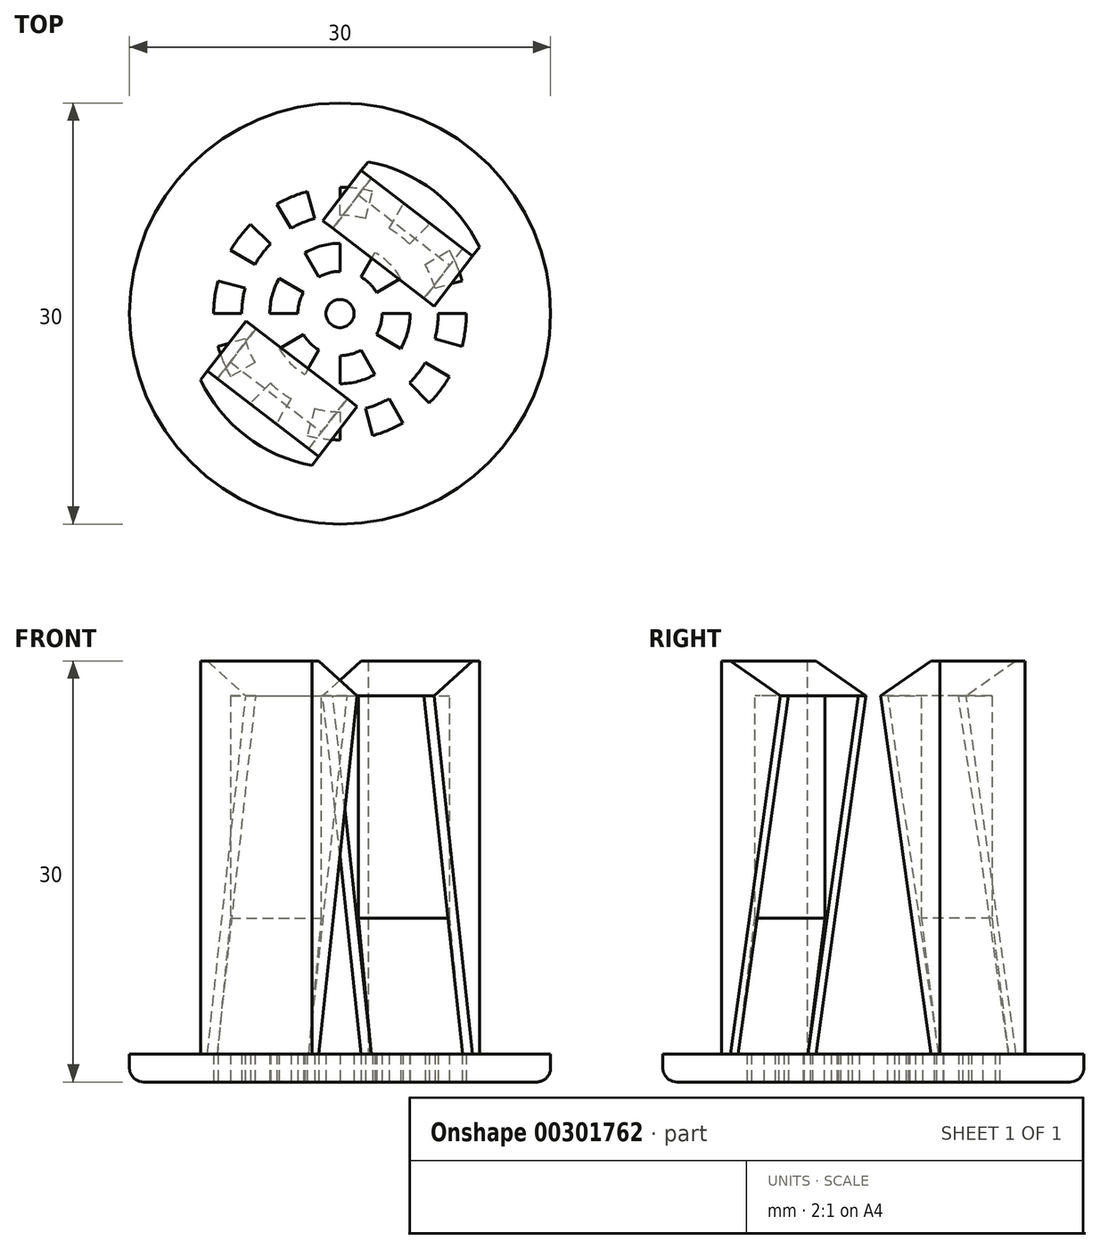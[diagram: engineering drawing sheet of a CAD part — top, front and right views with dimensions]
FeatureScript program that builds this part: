
annotation { "Feature Type Name" : "Feature", "Feature Type Description" : "" }
export const myFeature = defineFeature(function(context is Context, id is Id, definition is map)
    precondition{}
    {
        {
            var Q0;
            Q0=qCreatedBy(makeId("Top.planeOp"),FACE);
            var sketch = newSketch(context, id + "F0", { "sketchPlane" : qUnion([Q0])});
            skCircle(sketch, "E0", {"center": v(0, 0) * mm, "radius": 15 * mm});
            skCircle(sketch, "E1", {"center": v(0, 0) * mm, "radius": 1 * mm});
            skArc(sketch, "E2", {"start": v(-3, 0) * mm, "mid": v(-2.9, 0.78) * mm, "end": v(-2.6, 1.5) * mm});
            skLineSegment(sketch, "E3", {"start": v(-3, 0) * mm, "end": v(-5, 0) * mm});
            skLineSegment(sketch, "E4", {"start": v(-2.6, 1.5) * mm, "end": v(-4.33, 2.5) * mm});
            skArc(sketch, "E5", {"start": v(-5, 0) * mm, "mid": v(-4.83, 1.3) * mm, "end": v(-4.33, 2.5) * mm});
            skLineSegment(sketch, "E6.1.0", {"start": v(-2.6, -1.5) * mm, "end": v(-4.33, -2.5) * mm});
            skArc(sketch, "E6.1.1", {"start": v(-1.5, -2.6) * mm, "mid": v(-2.12, -2.12) * mm, "end": v(-2.6, -1.5) * mm});
            skLineSegment(sketch, "E6.1.2", {"start": v(-1.5, -2.6) * mm, "end": v(-2.5, -4.33) * mm});
            skArc(sketch, "E6.1.3", {"start": v(-2.5, -4.33) * mm, "mid": v(-3.54, -3.54) * mm, "end": v(-4.33, -2.5) * mm});
            skLineSegment(sketch, "E6.2.0", {"start": v(0, -3) * mm, "end": v(0, -5) * mm});
            skArc(sketch, "E6.2.1", {"start": v(1.5, -2.6) * mm, "mid": v(0.78, -2.9) * mm, "end": v(0, -3) * mm});
            skLineSegment(sketch, "E6.2.2", {"start": v(1.5, -2.6) * mm, "end": v(2.5, -4.33) * mm});
            skArc(sketch, "E6.2.3", {"start": v(2.5, -4.33) * mm, "mid": v(1.3, -4.83) * mm, "end": v(0, -5) * mm});
            skLineSegment(sketch, "E6.3.0", {"start": v(2.6, -1.5) * mm, "end": v(4.33, -2.5) * mm});
            skArc(sketch, "E6.3.1", {"start": v(3, 0) * mm, "mid": v(2.9, -0.78) * mm, "end": v(2.6, -1.5) * mm});
            skLineSegment(sketch, "E6.3.2", {"start": v(3, 0) * mm, "end": v(5, 0) * mm});
            skArc(sketch, "E6.3.3", {"start": v(5, 0) * mm, "mid": v(4.83, -1.3) * mm, "end": v(4.33, -2.5) * mm});
            skLineSegment(sketch, "E6.4.0", {"start": v(2.6, 1.5) * mm, "end": v(4.33, 2.5) * mm});
            skArc(sketch, "E6.4.1", {"start": v(1.5, 2.6) * mm, "mid": v(2.12, 2.12) * mm, "end": v(2.6, 1.5) * mm});
            skLineSegment(sketch, "E6.4.2", {"start": v(1.5, 2.6) * mm, "end": v(2.5, 4.33) * mm});
            skArc(sketch, "E6.4.3", {"start": v(2.5, 4.33) * mm, "mid": v(3.54, 3.54) * mm, "end": v(4.33, 2.5) * mm});
            skArc(sketch, "E7.3.5.0", {"start": v(-1.5, 2.6) * mm, "mid": v(-0.78, 2.9) * mm, "end": v(0, 3) * mm});
            skLineSegment(sketch, "E7.7.5.0", {"start": v(-1.5, 2.6) * mm, "end": v(-2.5, 4.33) * mm});
            skLineSegment(sketch, "E7.9.5.0", {"start": v(0, 3) * mm, "end": v(0, 5) * mm});
            skArc(sketch, "E7.10.5.0", {"start": v(-2.5, 4.33) * mm, "mid": v(-1.3, 4.83) * mm, "end": v(0, 5) * mm});
            skLineSegment(sketch, "E8", {"start": v(-7, 0) * mm, "end": v(-9, 0) * mm});
            skArc(sketch, "E9", {"start": v(-7, 0) * mm, "mid": v(-6.94, 0.91) * mm, "end": v(-6.76, 1.81) * mm});
            skArc(sketch, "E10", {"start": v(-9, 0) * mm, "mid": v(-8.92, 1.17) * mm, "end": v(-8.7, 2.33) * mm});
            skLineSegment(sketch, "E11", {"start": v(-6.76, 1.81) * mm, "end": v(-8.7, 2.33) * mm});
            skArc(sketch, "E12.1.0", {"start": v(-7.8, -4.5) * mm, "mid": v(-8.31, -3.44) * mm, "end": v(-8.7, -2.33) * mm});
            skLineSegment(sketch, "E12.1.1", {"start": v(-6.06, -3.5) * mm, "end": v(-7.8, -4.5) * mm});
            skLineSegment(sketch, "E12.1.2", {"start": v(-6.76, -1.81) * mm, "end": v(-8.7, -2.33) * mm});
            skArc(sketch, "E12.1.3", {"start": v(-6.06, -3.5) * mm, "mid": v(-6.47, -2.68) * mm, "end": v(-6.76, -1.81) * mm});
            skArc(sketch, "E12.2.0", {"start": v(-4.5, -7.8) * mm, "mid": v(-5.48, -7.14) * mm, "end": v(-6.36, -6.36) * mm});
            skLineSegment(sketch, "E12.2.1", {"start": v(-3.5, -6.06) * mm, "end": v(-4.5, -7.8) * mm});
            skLineSegment(sketch, "E12.2.2", {"start": v(-4.95, -4.95) * mm, "end": v(-6.36, -6.36) * mm});
            skArc(sketch, "E12.2.3", {"start": v(-3.5, -6.06) * mm, "mid": v(-4.26, -5.55) * mm, "end": v(-4.95, -4.95) * mm});
            skArc(sketch, "E12.3.0", {"start": v(0, -9) * mm, "mid": v(-1.17, -8.92) * mm, "end": v(-2.33, -8.7) * mm});
            skLineSegment(sketch, "E12.3.1", {"start": v(0, -7) * mm, "end": v(0, -9) * mm});
            skLineSegment(sketch, "E12.3.2", {"start": v(-1.81, -6.76) * mm, "end": v(-2.33, -8.7) * mm});
            skArc(sketch, "E12.3.3", {"start": v(0, -7) * mm, "mid": v(-0.91, -6.94) * mm, "end": v(-1.81, -6.76) * mm});
            skArc(sketch, "E12.4.0", {"start": v(4.5, -7.8) * mm, "mid": v(3.44, -8.31) * mm, "end": v(2.33, -8.7) * mm});
            skLineSegment(sketch, "E12.4.1", {"start": v(3.5, -6.06) * mm, "end": v(4.5, -7.8) * mm});
            skLineSegment(sketch, "E12.4.2", {"start": v(1.81, -6.76) * mm, "end": v(2.33, -8.7) * mm});
            skArc(sketch, "E12.4.3", {"start": v(3.5, -6.06) * mm, "mid": v(2.68, -6.47) * mm, "end": v(1.81, -6.76) * mm});
            skArc(sketch, "E12.5.0", {"start": v(7.8, -4.5) * mm, "mid": v(7.14, -5.48) * mm, "end": v(6.36, -6.36) * mm});
            skLineSegment(sketch, "E12.5.1", {"start": v(6.06, -3.5) * mm, "end": v(7.8, -4.5) * mm});
            skLineSegment(sketch, "E12.5.2", {"start": v(4.95, -4.95) * mm, "end": v(6.36, -6.36) * mm});
            skArc(sketch, "E12.5.3", {"start": v(6.06, -3.5) * mm, "mid": v(5.55, -4.26) * mm, "end": v(4.95, -4.95) * mm});
            skArc(sketch, "E12.6.0", {"start": v(9, 0) * mm, "mid": v(8.92, -1.17) * mm, "end": v(8.7, -2.33) * mm});
            skLineSegment(sketch, "E12.6.1", {"start": v(7, 0) * mm, "end": v(9, 0) * mm});
            skLineSegment(sketch, "E12.6.2", {"start": v(6.76, -1.81) * mm, "end": v(8.7, -2.33) * mm});
            skArc(sketch, "E12.6.3", {"start": v(7, 0) * mm, "mid": v(6.94, -0.91) * mm, "end": v(6.76, -1.81) * mm});
            skArc(sketch, "E12.7.0", {"start": v(7.8, 4.5) * mm, "mid": v(8.31, 3.44) * mm, "end": v(8.7, 2.33) * mm});
            skLineSegment(sketch, "E12.7.1", {"start": v(6.06, 3.5) * mm, "end": v(7.8, 4.5) * mm});
            skLineSegment(sketch, "E12.7.2", {"start": v(6.76, 1.81) * mm, "end": v(8.7, 2.33) * mm});
            skArc(sketch, "E12.7.3", {"start": v(6.06, 3.5) * mm, "mid": v(6.47, 2.68) * mm, "end": v(6.76, 1.81) * mm});
            skArc(sketch, "E12.8.0", {"start": v(4.5, 7.8) * mm, "mid": v(5.48, 7.14) * mm, "end": v(6.36, 6.36) * mm});
            skLineSegment(sketch, "E12.8.1", {"start": v(3.5, 6.06) * mm, "end": v(4.5, 7.8) * mm});
            skLineSegment(sketch, "E12.8.2", {"start": v(4.95, 4.95) * mm, "end": v(6.36, 6.36) * mm});
            skArc(sketch, "E12.8.3", {"start": v(3.5, 6.06) * mm, "mid": v(4.26, 5.55) * mm, "end": v(4.95, 4.95) * mm});
            skArc(sketch, "E12.9.0", {"start": v(0, 9) * mm, "mid": v(1.17, 8.92) * mm, "end": v(2.33, 8.7) * mm});
            skLineSegment(sketch, "E12.9.1", {"start": v(0, 7) * mm, "end": v(0, 9) * mm});
            skLineSegment(sketch, "E12.9.2", {"start": v(1.81, 6.76) * mm, "end": v(2.33, 8.7) * mm});
            skArc(sketch, "E12.9.3", {"start": v(0, 7) * mm, "mid": v(0.91, 6.94) * mm, "end": v(1.81, 6.76) * mm});
            skArc(sketch, "E12.10.0", {"start": v(-4.5, 7.8) * mm, "mid": v(-3.44, 8.31) * mm, "end": v(-2.33, 8.7) * mm});
            skLineSegment(sketch, "E12.10.1", {"start": v(-3.5, 6.06) * mm, "end": v(-4.5, 7.8) * mm});
            skLineSegment(sketch, "E12.10.2", {"start": v(-1.81, 6.76) * mm, "end": v(-2.33, 8.7) * mm});
            skArc(sketch, "E12.10.3", {"start": v(-3.5, 6.06) * mm, "mid": v(-2.68, 6.47) * mm, "end": v(-1.81, 6.76) * mm});
            skArc(sketch, "E12.11.0", {"start": v(-7.8, 4.5) * mm, "mid": v(-7.14, 5.48) * mm, "end": v(-6.36, 6.36) * mm});
            skLineSegment(sketch, "E12.11.1", {"start": v(-6.06, 3.5) * mm, "end": v(-7.8, 4.5) * mm});
            skLineSegment(sketch, "E12.11.2", {"start": v(-4.95, 4.95) * mm, "end": v(-6.36, 6.36) * mm});
            skArc(sketch, "E12.11.3", {"start": v(-6.06, 3.5) * mm, "mid": v(-5.55, 4.26) * mm, "end": v(-4.95, 4.95) * mm});
            skSolve(sketch);
        }
        {
            var Q0;
            Q0=makeQuery(id+"F0.imprint","IMPRINT",FACE,{"disambiguationData":[TD([[makeQuery(id+"F0.imprint","IMPRINT",EDGE,{"derivedFrom":sQuery(id+"F0.wireOp",EDGE,"E0")}),1.0]])]});
            extrude(context, id + "F1", {"entities" : qUnion([Q0]), "depth" : 2 * mm});
        }
        {
            var Q0;
            Q0=makeQuery(id+"F1.opExtrude","CAP_FACE",FACE,{"disambiguationData":[OSD([sQuery(id+"F0.wireOp",EDGE,"E0"),sQuery(id+"F0.wireOp",EDGE,"E1"),sQuery(id+"F0.wireOp",EDGE,"E2"),sQuery(id+"F0.wireOp",EDGE,"E3"),sQuery(id+"F0.wireOp",EDGE,"E4"),sQuery(id+"F0.wireOp",EDGE,"E5"),sQuery(id+"F0.wireOp",EDGE,"E6.1.0"),sQuery(id+"F0.wireOp",EDGE,"E6.1.1"),sQuery(id+"F0.wireOp",EDGE,"E6.1.2"),sQuery(id+"F0.wireOp",EDGE,"E6.1.3"),sQuery(id+"F0.wireOp",EDGE,"E6.2.0"),sQuery(id+"F0.wireOp",EDGE,"E6.2.1"),sQuery(id+"F0.wireOp",EDGE,"E6.2.2"),sQuery(id+"F0.wireOp",EDGE,"E6.2.3"),sQuery(id+"F0.wireOp",EDGE,"E6.3.0"),sQuery(id+"F0.wireOp",EDGE,"E6.3.1"),sQuery(id+"F0.wireOp",EDGE,"E6.3.2"),sQuery(id+"F0.wireOp",EDGE,"E6.3.3"),sQuery(id+"F0.wireOp",EDGE,"E6.4.0"),sQuery(id+"F0.wireOp",EDGE,"E6.4.1"),sQuery(id+"F0.wireOp",EDGE,"E6.4.2"),sQuery(id+"F0.wireOp",EDGE,"E6.4.3"),sQuery(id+"F0.wireOp",EDGE,"E7.3.5.0"),sQuery(id+"F0.wireOp",EDGE,"E7.7.5.0"),sQuery(id+"F0.wireOp",EDGE,"E7.9.5.0"),sQuery(id+"F0.wireOp",EDGE,"E7.10.5.0"),sQuery(id+"F0.wireOp",EDGE,"E8"),sQuery(id+"F0.wireOp",EDGE,"E9"),sQuery(id+"F0.wireOp",EDGE,"E10"),sQuery(id+"F0.wireOp",EDGE,"E11"),sQuery(id+"F0.wireOp",EDGE,"E12.1.0"),sQuery(id+"F0.wireOp",EDGE,"E12.1.1"),sQuery(id+"F0.wireOp",EDGE,"E12.1.2"),sQuery(id+"F0.wireOp",EDGE,"E12.1.3"),sQuery(id+"F0.wireOp",EDGE,"E12.2.0"),sQuery(id+"F0.wireOp",EDGE,"E12.2.1"),sQuery(id+"F0.wireOp",EDGE,"E12.2.2"),sQuery(id+"F0.wireOp",EDGE,"E12.2.3"),sQuery(id+"F0.wireOp",EDGE,"E12.3.0"),sQuery(id+"F0.wireOp",EDGE,"E12.3.1"),sQuery(id+"F0.wireOp",EDGE,"E12.3.2"),sQuery(id+"F0.wireOp",EDGE,"E12.3.3"),sQuery(id+"F0.wireOp",EDGE,"E12.4.0"),sQuery(id+"F0.wireOp",EDGE,"E12.4.1"),sQuery(id+"F0.wireOp",EDGE,"E12.4.2"),sQuery(id+"F0.wireOp",EDGE,"E12.4.3"),sQuery(id+"F0.wireOp",EDGE,"E12.5.0"),sQuery(id+"F0.wireOp",EDGE,"E12.5.1"),sQuery(id+"F0.wireOp",EDGE,"E12.5.2"),sQuery(id+"F0.wireOp",EDGE,"E12.5.3"),sQuery(id+"F0.wireOp",EDGE,"E12.6.0"),sQuery(id+"F0.wireOp",EDGE,"E12.6.1"),sQuery(id+"F0.wireOp",EDGE,"E12.6.2"),sQuery(id+"F0.wireOp",EDGE,"E12.6.3"),sQuery(id+"F0.wireOp",EDGE,"E12.7.0"),sQuery(id+"F0.wireOp",EDGE,"E12.7.1"),sQuery(id+"F0.wireOp",EDGE,"E12.7.2"),sQuery(id+"F0.wireOp",EDGE,"E12.7.3"),sQuery(id+"F0.wireOp",EDGE,"E12.8.0"),sQuery(id+"F0.wireOp",EDGE,"E12.8.1"),sQuery(id+"F0.wireOp",EDGE,"E12.8.2"),sQuery(id+"F0.wireOp",EDGE,"E12.8.3"),sQuery(id+"F0.wireOp",EDGE,"E12.9.0"),sQuery(id+"F0.wireOp",EDGE,"E12.9.1"),sQuery(id+"F0.wireOp",EDGE,"E12.9.2"),sQuery(id+"F0.wireOp",EDGE,"E12.9.3"),sQuery(id+"F0.wireOp",EDGE,"E12.10.0"),sQuery(id+"F0.wireOp",EDGE,"E12.10.1"),sQuery(id+"F0.wireOp",EDGE,"E12.10.2"),sQuery(id+"F0.wireOp",EDGE,"E12.10.3"),sQuery(id+"F0.wireOp",EDGE,"E12.11.0"),sQuery(id+"F0.wireOp",EDGE,"E12.11.1"),sQuery(id+"F0.wireOp",EDGE,"E12.11.2"),sQuery(id+"F0.wireOp",EDGE,"E12.11.3")])],"isStart":false});
            var sketch = newSketch(context, id + "F2", { "sketchPlane" : qUnion([Q0])});
            skLineSegment(sketch, "E13", {"start": v(1.51, 10.18) * mm, "end": v(9.45, 4.1) * mm});
            skLineSegment(sketch, "E14", {"start": v(9.45, 4.1) * mm, "end": v(10.66, 5.68) * mm});
            skLineSegment(sketch, "E15", {"start": v(10.66, 5.68) * mm, "end": v(2.73, 11.77) * mm});
            skLineSegment(sketch, "E16", {"start": v(2.73, 11.77) * mm, "end": v(1.51, 10.18) * mm});
            skLineSegment(sketch, "E17.1.0", {"start": v(-1.51, -10.18) * mm, "end": v(-9.45, -4.1) * mm});
            skLineSegment(sketch, "E17.1.1", {"start": v(-10.66, -5.68) * mm, "end": v(-2.73, -11.77) * mm});
            skLineSegment(sketch, "E17.1.2", {"start": v(-2.73, -11.77) * mm, "end": v(-1.51, -10.18) * mm});
            skLineSegment(sketch, "E17.1.3", {"start": v(-9.45, -4.1) * mm, "end": v(-10.66, -5.68) * mm});
            skPoint(sketch, "E17.center", {"position": v(0, 0) * mm});
            skCircle(sketch, "E18", {"center": v(0, 0) * mm, "radius": 11 * mm});
            skLineSegment(sketch, "E19", {"start": v(0, 0) * mm, "end": v(2.33, -8.7) * mm});
            skLineSegment(sketch, "E20", {"start": v(0, 0) * mm, "end": v(6.7, 8.73) * mm});
            skSolve(sketch);
        }
        {
            var Q0;
            {var subQ1=sQuery(id+"F2.wireOp",EDGE,"E13");var subQ3=sQuery(id+"F2.wireOp",EDGE,"E14");var subQ4=makeQuery(id+"F2.imprint","INTERSECT",VERTEX,{"derivedFrom":[subQ1,subQ3]});Q0=makeQuery(id+"F2.imprint","IMPRINT",FACE,{"disambiguationData":[TD([[makeQuery(id+"F2.imprint","IMPRINT",EDGE,{"disambiguationData":[TD([[subQ4,-1.0]])],"derivedFrom":subQ3}),1.0]])]});}
            var Q1;
            {var subQ1=sQuery(id+"F2.wireOp",EDGE,"E13");var subQ3=sQuery(id+"F2.wireOp",EDGE,"E16");var subQ4=makeQuery(id+"F2.imprint","INTERSECT",VERTEX,{"derivedFrom":[subQ1,subQ3]});Q1=makeQuery(id+"F2.imprint","IMPRINT",FACE,{"disambiguationData":[TD([[makeQuery(id+"F2.imprint","IMPRINT",EDGE,{"disambiguationData":[TD([[subQ4,1.0]])],"derivedFrom":subQ3}),1.0]])]});}
            var Q2;
            {var subQ1=sQuery(id+"F2.wireOp",EDGE,"E17.1.0");var subQ6=sQuery(id+"F2.wireOp",EDGE,"E17.1.2");var subQ7=makeQuery(id+"F2.imprint","INTERSECT",VERTEX,{"derivedFrom":[subQ1,subQ6]});Q2=makeQuery(id+"F2.imprint","IMPRINT",FACE,{"disambiguationData":[TD([[makeQuery(id+"F2.imprint","IMPRINT",EDGE,{"disambiguationData":[TD([[subQ7,1.0]])],"derivedFrom":subQ6}),1.0]])]});}
            extrude(context, id + "F3", {"entities" : qUnion([Q0, Q1, Q2]), "operationType" : NewBodyOperationType.ADD, "depth" : 28 * mm});
        }
        {
            var Q0;
            Q0=makeQuery(id+"F3.opExtrude","SWEPT_FACE",FACE,{"disambiguationData":[OSD([sQuery(id+"F2.wireOp",EDGE,"E17.1.2")])]});
            var sketch = newSketch(context, id + "F4", { "sketchPlane" : qUnion([Q0])});
            skLineSegment(sketch, "E21", {"start": v(-9, 30) * mm, "end": v(-4.5, 27.5) * mm});
            skLineSegment(sketch, "E22", {"start": v(-4.5, 27.5) * mm, "end": v(-7.5, 27.5) * mm});
            skLineSegment(sketch, "E23", {"start": v(-7.5, 27.5) * mm, "end": v(-7.5, 11.69) * mm});
            skLineSegment(sketch, "E24", {"start": v(-7.5, 11.69) * mm, "end": v(-9, 2) * mm});
            skLineSegment(sketch, "E25", {"start": v(-9, 30) * mm, "end": v(-9, 2) * mm});
            skLineSegment(sketch, "E26", {"start": v(0, 0) * mm, "end": v(0, 31.02) * mm});
            skLineSegment(sketch, "E27.MirrorCS", {"start": v(7.5, 27.5) * mm, "end": v(7.5, 11.69) * mm});
            skLineSegment(sketch, "E28.MirrorCS", {"start": v(9, 30) * mm, "end": v(9, 2) * mm});
            skLineSegment(sketch, "E29.MirrorCS", {"start": v(9, 30) * mm, "end": v(4.5, 27.5) * mm});
            skLineSegment(sketch, "E30.MirrorCS", {"start": v(7.5, 11.69) * mm, "end": v(9, 2) * mm});
            skLineSegment(sketch, "E31.MirrorCS", {"start": v(4.5, 27.5) * mm, "end": v(7.5, 27.5) * mm});
            skSolve(sketch);
        }
        {
            var Q0;
            Q0 = qSketchRegion(id + "F4", true);
            extrude(context, id + "F5", {"entities" : qUnion([Q0]), "operationType" : NewBodyOperationType.ADD, "oppositeDirection" : true, "depth" : 10 * mm});
        }
        {
            var Q0;
            Q0=makeQuery(id+"F5.boolean.opBoolean","MERGE",FACE,{"derivedFrom":[makeQuery(id+"F3.opExtrude","SWEPT_FACE",FACE,{"disambiguationData":[OSD([sQuery(id+"F2.wireOp",EDGE,"E17.1.2")])]}),makeQuery(id+"F5.opExtrude","CAP_FACE",FACE,{"disambiguationData":[OSD([sQuery(id+"F4.wireOp",EDGE,"E21"),sQuery(id+"F4.wireOp",EDGE,"E22"),sQuery(id+"F4.wireOp",EDGE,"E23"),sQuery(id+"F4.wireOp",EDGE,"E24"),sQuery(id+"F4.wireOp",EDGE,"E25")])],"isStart":true})]});
            var sketch = newSketch(context, id + "F6", { "sketchPlane" : qUnion([Q0])});
            skLineSegment(sketch, "E32", {"start": v(-4.5, 27.5) * mm, "end": v(-7.5, 27.5) * mm});
            skLineSegment(sketch, "E33", {"start": v(-7.5, 27.5) * mm, "end": v(-7.5, 22.8) * mm});
            skLineSegment(sketch, "E34", {"start": v(0, 2) * mm, "end": v(0, 41.24) * mm});
            skLineSegment(sketch, "E35", {"start": v(-7.5, 22.8) * mm, "end": v(-9, 2) * mm});
            skLineSegment(sketch, "E36", {"start": v(-9, 2) * mm, "end": v(-4.5, 27.5) * mm});
            skLineSegment(sketch, "E37.MirrorCS", {"start": v(7.5, 27.5) * mm, "end": v(7.5, 22.8) * mm});
            skLineSegment(sketch, "E38.MirrorCS", {"start": v(4.5, 27.5) * mm, "end": v(7.5, 27.5) * mm});
            skLineSegment(sketch, "E39.MirrorCS", {"start": v(9, 2) * mm, "end": v(4.5, 27.5) * mm});
            skLineSegment(sketch, "E40.MirrorCS", {"start": v(7.5, 22.8) * mm, "end": v(9, 2) * mm});
            skSolve(sketch);
        }
        {
            var Q0;
            Q0 = qSketchRegion(id + "F6", true);
            extrude(context, id + "F7", {"entities" : qUnion([Q0]), "operationType" : NewBodyOperationType.ADD, "oppositeDirection" : true, "depth" : 0.9 * mm});
        }
        {
            var Q0;
            Q0=makeQuery(id+"F5.boolean.opBoolean","MERGE",FACE,{"derivedFrom":[makeQuery(id+"F3.opExtrude","SWEPT_FACE",FACE,{"disambiguationData":[OSD([sQuery(id+"F2.wireOp",EDGE,"E16")])]}),makeQuery(id+"F5.opExtrude","CAP_FACE",FACE,{"disambiguationData":[OSD([sQuery(id+"F4.wireOp",EDGE,"E27.MirrorCS"),sQuery(id+"F4.wireOp",EDGE,"E28.MirrorCS"),sQuery(id+"F4.wireOp",EDGE,"E29.MirrorCS"),sQuery(id+"F4.wireOp",EDGE,"E30.MirrorCS"),sQuery(id+"F4.wireOp",EDGE,"E31.MirrorCS")])],"isStart":false})]});
            var sketch = newSketch(context, id + "F8", { "sketchPlane" : qUnion([Q0])});
            skLineSegment(sketch, "E41", {"start": v(-4.5, 27.5) * mm, "end": v(-7.5, 27.5) * mm});
            skLineSegment(sketch, "E42", {"start": v(-7.5, 27.5) * mm, "end": v(-7.5, 11.69) * mm});
            skLineSegment(sketch, "E43", {"start": v(0, 2) * mm, "end": v(0, 35.25) * mm});
            skLineSegment(sketch, "E44", {"start": v(-7.5, 11.69) * mm, "end": v(-9, 2) * mm});
            skLineSegment(sketch, "E45", {"start": v(-9, 2) * mm, "end": v(-4.5, 27.5) * mm});
            skLineSegment(sketch, "E46.MirrorCS", {"start": v(4.5, 27.5) * mm, "end": v(7.5, 27.5) * mm});
            skLineSegment(sketch, "E47.MirrorCS", {"start": v(9, 2) * mm, "end": v(4.5, 27.5) * mm});
            skLineSegment(sketch, "E48.MirrorCS", {"start": v(7.5, 27.5) * mm, "end": v(7.5, 11.69) * mm});
            skLineSegment(sketch, "E49.MirrorCS", {"start": v(7.5, 11.69) * mm, "end": v(9, 2) * mm});
            skSolve(sketch);
        }
        {
            var Q0;
            Q0 = qSketchRegion(id + "F8", true);
            extrude(context, id + "F9", {"entities" : qUnion([Q0]), "operationType" : NewBodyOperationType.ADD, "oppositeDirection" : true, "depth" : 0.9 * mm});
        }
        {
            var Q0;
            Q0=makeQuery(id+"F1.opExtrude","CAP_EDGE",EDGE,{"disambiguationData":[OSD([sQuery(id+"F0.wireOp",EDGE,"E0")])],"isStart":true});
            fillet(context, id + "F10", {"entities" : qUnion([Q0]), "radius" : 1 * mm, "tangentPropagation" : true, "allowEdgeOverflow" : false});
        }
    });
